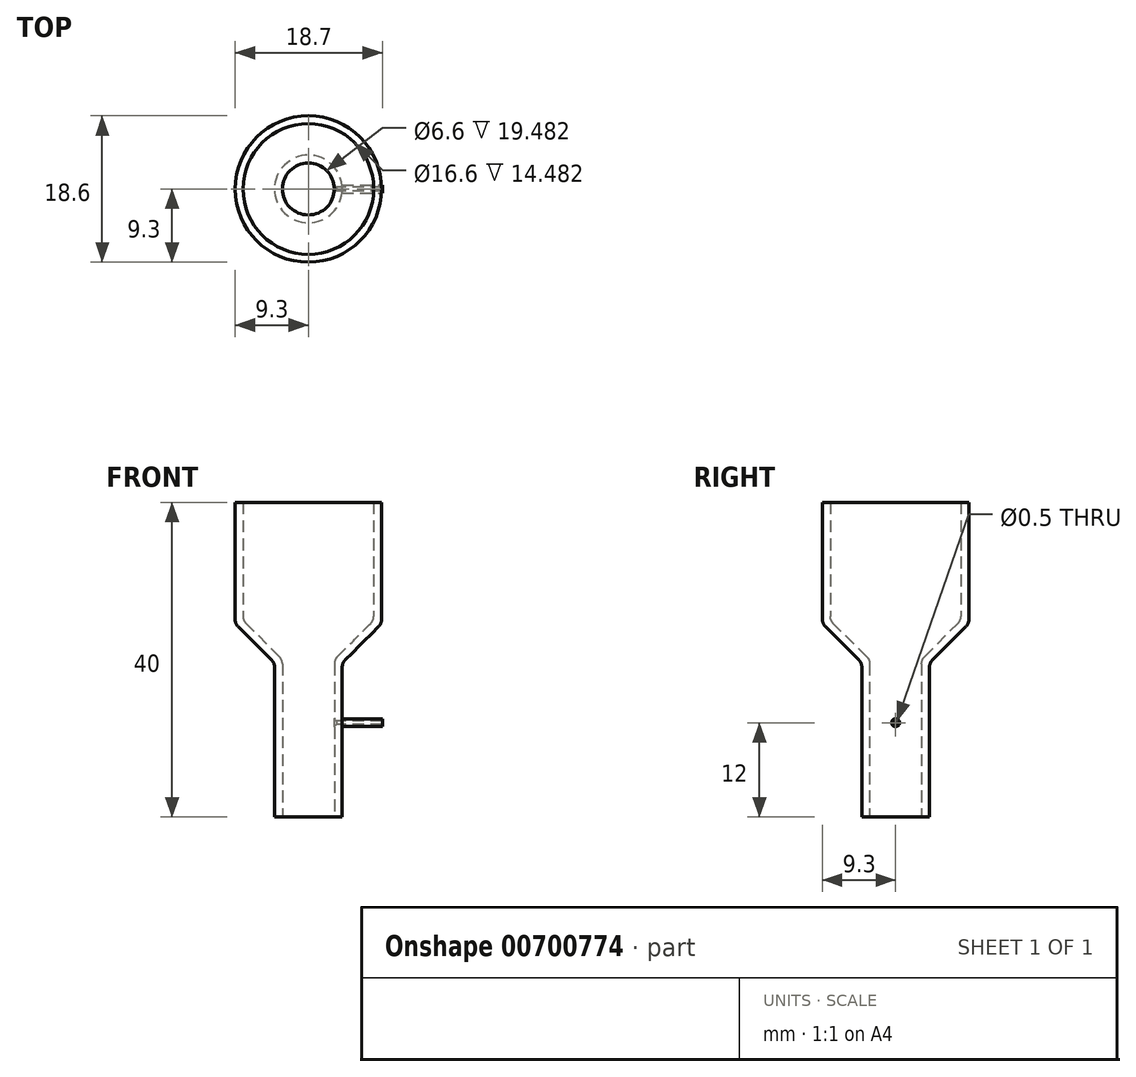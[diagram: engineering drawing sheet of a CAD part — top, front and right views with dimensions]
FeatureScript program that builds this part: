
annotation { "Feature Type Name" : "Feature", "Feature Type Description" : "" }
export const myFeature = defineFeature(function(context is Context, id is Id, definition is map)
    precondition{}
    {
        {
            var Q0;
            Q0=qCreatedBy(makeId("Front.planeOp"),FACE);
            var sketch = newSketch(context, id + "F0", { "sketchPlane" : qUnion([Q0])});
            skLineSegment(sketch, "E0", {"start": v(-3.3, 0) * mm, "end": v(-3.3, 20) * mm});
            skLineSegment(sketch, "E1", {"start": v(-8.3, 25) * mm, "end": v(-8.3, 40) * mm});
            skLineSegment(sketch, "E2", {"start": v(-8.3, 25) * mm, "end": v(-3.3, 20) * mm});
            skLineSegment(sketch, "E3.0", {"start": v(-4.3, 0) * mm, "end": v(-4.3, 19.59) * mm});
            skLineSegment(sketch, "E3.1", {"start": v(-9.3, 24.59) * mm, "end": v(-4.3, 19.59) * mm});
            skLineSegment(sketch, "E3.2", {"start": v(-9.3, 24.59) * mm, "end": v(-9.3, 40) * mm});
            skLineSegment(sketch, "E4", {"start": v(-9.3, 40) * mm, "end": v(-8.3, 40) * mm});
            skLineSegment(sketch, "E5", {"start": v(-4.3, 0) * mm, "end": v(-3.3, 0) * mm});
            skLineSegment(sketch, "E6", {"start": v(0, 0) * mm, "end": v(0, 18.79) * mm});
            skSolve(sketch);
        }
        {
            var Q0;
            Q0=makeQuery(id+"F0.imprint","IMPRINT",FACE,{"disambiguationData":[TD([[makeQuery(id+"F0.imprint","IMPRINT",EDGE,{"derivedFrom":sQuery(id+"F0.wireOp",EDGE,"E0")}),1.0]])]});
            var Q1;
            Q1=sQuery(id+"F0.wireOp",EDGE,"E6");
            revolve(context, id + "F1", {"entities" : qUnion([Q0]), "axis" : qUnion([Q1]), "revolveType" : RevolveType.FULL});
        }
        {
            var Q0;
            Q0=makeQuery(id+"F1.opRevolve","SWEPT_EDGE",EDGE,{"disambiguationData":[OSD([sQuery(id+"F0.wireOp",EDGE,"E3.1"),sQuery(id+"F0.wireOp",EDGE,"E3.2")])]});
            var Q1;
            Q1=makeQuery(id+"F1.opRevolve","SWEPT_EDGE",EDGE,{"disambiguationData":[OSD([sQuery(id+"F0.wireOp",EDGE,"E3.0"),sQuery(id+"F0.wireOp",EDGE,"E3.1")])]});
            var Q2;
            Q2=makeQuery(id+"F1.opRevolve","SWEPT_EDGE",EDGE,{"disambiguationData":[OSD([sQuery(id+"F0.wireOp",EDGE,"E1"),sQuery(id+"F0.wireOp",EDGE,"E2")])]});
            var Q3;
            Q3=makeQuery(id+"F1.opRevolve","SWEPT_EDGE",EDGE,{"disambiguationData":[OSD([sQuery(id+"F0.wireOp",EDGE,"E0"),sQuery(id+"F0.wireOp",EDGE,"E2")])]});
            fillet(context, id + "F2", {"entities" : qUnion([Q0, Q1, Q2, Q3]), "radius" : 1.25 * mm, "tangentPropagation" : true, "allowEdgeOverflow" : false});
        }
        {
            var Q0;
            Q0=qCreatedBy(makeId("Right.planeOp"),FACE);
            cPlane(context, id + "F3", {"entities" : qUnion([Q0]), "cplaneType" : CPlaneType.OFFSET, "offset" : 9.4 * mm, "width" : 150 * mm, "height" : 150 * mm});
        }
        {
            var Q0;
            Q0=qCreatedBy(makeId("Right.planeOp"),FACE);
            var sketch = newSketch(context, id + "F4", { "sketchPlane" : qUnion([Q0])});
            skCircle(sketch, "E7", {"center": v(0, 12) * mm, "radius": 0.25 * mm});
            skSolve(sketch);
        }
        {
            var Q0;
            Q0 = qSketchRegion(id + "F4", true);
            var Q1;
            Q1=qCreatedBy(id+"F3.planeOp",FACE);
            extrude(context, id + "F5", {"entities" : qUnion([Q0]), "operationType" : NewBodyOperationType.REMOVE, "endBound" : BoundingType.UP_TO_SURFACE, "depth" : 25 * mm, "endBoundEntityFace" : qUnion([Q1]), "offsetDistance" : 25 * mm});
        }
        {
            var Q0;
            Q0=qCreatedBy(id+"F3.planeOp",FACE);
            var sketch = newSketch(context, id + "F6", { "sketchPlane" : qUnion([Q0])});
            skCircle(sketch, "E8", {"center": v(0, 12) * mm, "radius": 0.25 * mm});
            skCircle(sketch, "E9", {"center": v(0, 12) * mm, "radius": 0.5 * mm});
            skSolve(sketch);
        }
        {
            var Q0;
            Q0=makeQuery(id+"F6.imprint","IMPRINT",FACE,{"disambiguationData":[TD([[makeQuery(id+"F6.imprint","IMPRINT",EDGE,{"derivedFrom":sQuery(id+"F6.wireOp",EDGE,"E8")}),-1.0]])]});
            var Q1;
            Q1=makeQuery(id+"F1.opRevolve","SWEPT_FACE",FACE,{"disambiguationData":[OSD([sQuery(id+"F0.wireOp",EDGE,"E3.0")])]});
            extrude(context, id + "F7", {"entities" : qUnion([Q0]), "operationType" : NewBodyOperationType.ADD, "endBound" : BoundingType.UP_TO_SURFACE, "oppositeDirection" : true, "depth" : 25 * mm, "endBoundEntityFace" : qUnion([Q1]), "offsetDistance" : 25 * mm});
        }
        {
            var Q0;
            Q0=makeQuery(id+"F7.opExtrude","CAP_EDGE",EDGE,{"disambiguationData":[OSD([sQuery(id+"F6.wireOp",EDGE,"E9")])],"isStart":false});
            var Q1;
            Q1=makeQuery(id+"F5.boolean.opBoolean","INTERSECT",EDGE,{"derivedFrom":[makeQuery(id+"F1.opRevolve","SWEPT_FACE",FACE,{"disambiguationData":[OSD([sQuery(id+"F0.wireOp",EDGE,"E0")])]}),makeQuery(id+"F5.opExtrude","SWEPT_FACE",FACE,{"disambiguationData":[OSD([sQuery(id+"F4.wireOp",EDGE,"E7")])]})]});
            fillet(context, id + "F8", {"entities" : qUnion([Q0, Q1]), "radius" : 0.3 * mm, "tangentPropagation" : true, "allowEdgeOverflow" : false});
        }
    });
